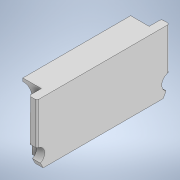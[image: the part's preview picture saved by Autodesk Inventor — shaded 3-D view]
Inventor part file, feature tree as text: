
AUTODESK INVENTOR PART (.ipt)
format: ipt  version: 2021.1 (Build 251245010, 245A)  size: 210,432 bytes
history: native  units: mm
features: extrude x4, sketch x4, fillet x1
ambient origin geometry x8: Origin, YZ Plane, XZ Plane, XY Plane, X Axis, Y Axis, Z Axis, Center Point
bodies: Volumenkörper1 (feature_tree)
feature tree (9):
  extrude  "Extrusion1"  Depth=21.5mm
  extrude  "Extrusion2"  Depth=2.0mm
  extrude  "Extrusion3"  Depth=10.0mm TaperAngle=0.0deg
  extrude  "Extrusion4"  Depth=0.3mm
  fillet  "Rundung1"  Radius=0.5mm
  sketch  "Skizze1"  dims[d0=1.3mm d1=21.5mm]
  sketch  "Skizze3"  dims[d2=1.5mm d3=2.0mm]
  sketch  "Skizze4"  dims[d4=2.0mm d5=10.0mm d6=0.0mm]
  sketch  "Skizze5"  dims[d7=0.4mm d8=0.0mm d9=1.5mm d10=0.5mm d11=1.5mm d12=18.0mm d13=0.0mm d14=8.0mm d15=2.5mm d16=2.5mm d17=18.0mm d18=0.0mm d19=0.3mm]
